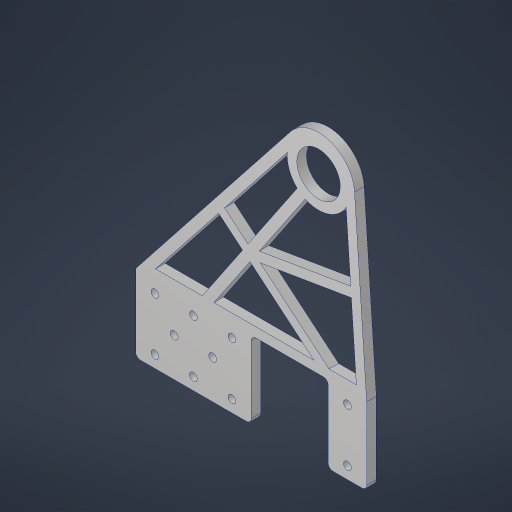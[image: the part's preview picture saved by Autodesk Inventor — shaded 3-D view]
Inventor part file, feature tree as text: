
AUTODESK INVENTOR PART (.ipt)
format: ipt  version: 2023.4 (Build 274418000, 418)  size: 309,248 bytes
history: native  units: in
note: dims shown in document units (in); Inventor stores cm internally (conversion verified against a paired STEP export)
features: sketch x3, extrude x2, hole x1, fillet x1, projected_geometry x1
ambient origin geometry x8: Origin, YZ Plane, XZ Plane, XY Plane, X Axis, Y Axis, Z Axis, Center Point
bodies: Solid1 (feature_tree)
feature tree (8):
  sketch  "Sketch1"  dims[d0=6.0in d1=2.0in]
  sketch  "Sketch2"  dims[d2=1.375in d3=0.5in d4=1.25in]
  extrude  "Extrusion1"  Depth=2.0in
  hole  "Hole1"  [1 undecoded]
  fillet  "Fillet1"  Radius=1.25in
  extrude  "Extrusion2"  Depth=0.125in
  sketch  "Sketch3"  dims[d5=1.25in d6=1.375in d7=1.0in d8=0.375in d9=0.5in d10=0.5in d11=0.5in d12=0.5in d13=0.5in d14=4.38in d15=5.0in d16=3.0in d17=1.125in d18=0.375in d20=0.375in d21=0.375in d22=0.25in d23=0.0in d24=0.201in d25=0.75in d26=0.375in d27=0.25in d28=0.5635in d29=1.0in d30=0.8108in d31=6.5in d32=0.75in d33=0.125in d34=0.25in d35=0.25in d36=0.125in d37=0.125in d38=0.125in d39=0.125in d40=0.125in d41=0.125in d42=0.0in d43=0.0in]
  projected_geometry  "Project Cut Edges1"
note: 1 required parameter value undecoded (feature->parameter linkage not recoverable at this tier; creation-order binding heuristic only, values carry confidence <= 0.55)
